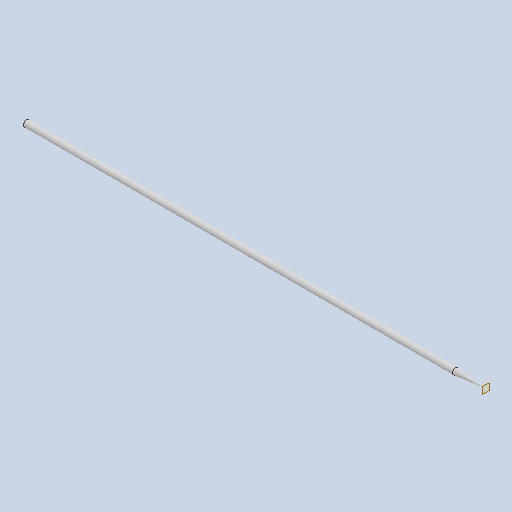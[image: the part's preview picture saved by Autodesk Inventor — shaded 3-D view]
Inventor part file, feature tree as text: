
AUTODESK INVENTOR PART (.ipt)
format: ipt  version: 2023 (Build 270158000, 158)  size: 142,336 bytes
history: native  units: mm
features: sketch x2, extrude x1, plane x1, loft x1, other x1
ambient origin geometry x8: Origin, YZ Plane, XZ Plane, XY Plane, X Axis, Y Axis, Z Axis, Center Point
bodies: Solid1 (feature_tree)
feature tree (6):
  extrude  "Extrusion1"  Depth=35.5mm TaperAngle=0.0deg
  plane  "Work Plane1"
  loft  "Loft1"
  sketch  "Sketch1"  dims[d0=0.51mm d1=35.5mm d2=0.0mm]
  sketch  "Sketch2"  dims[d3=2.5mm d4=0.001mm d5=0.0mm d6=90.0deg d7=0.0mm d8=90.0deg]
  other  "Edges1"
